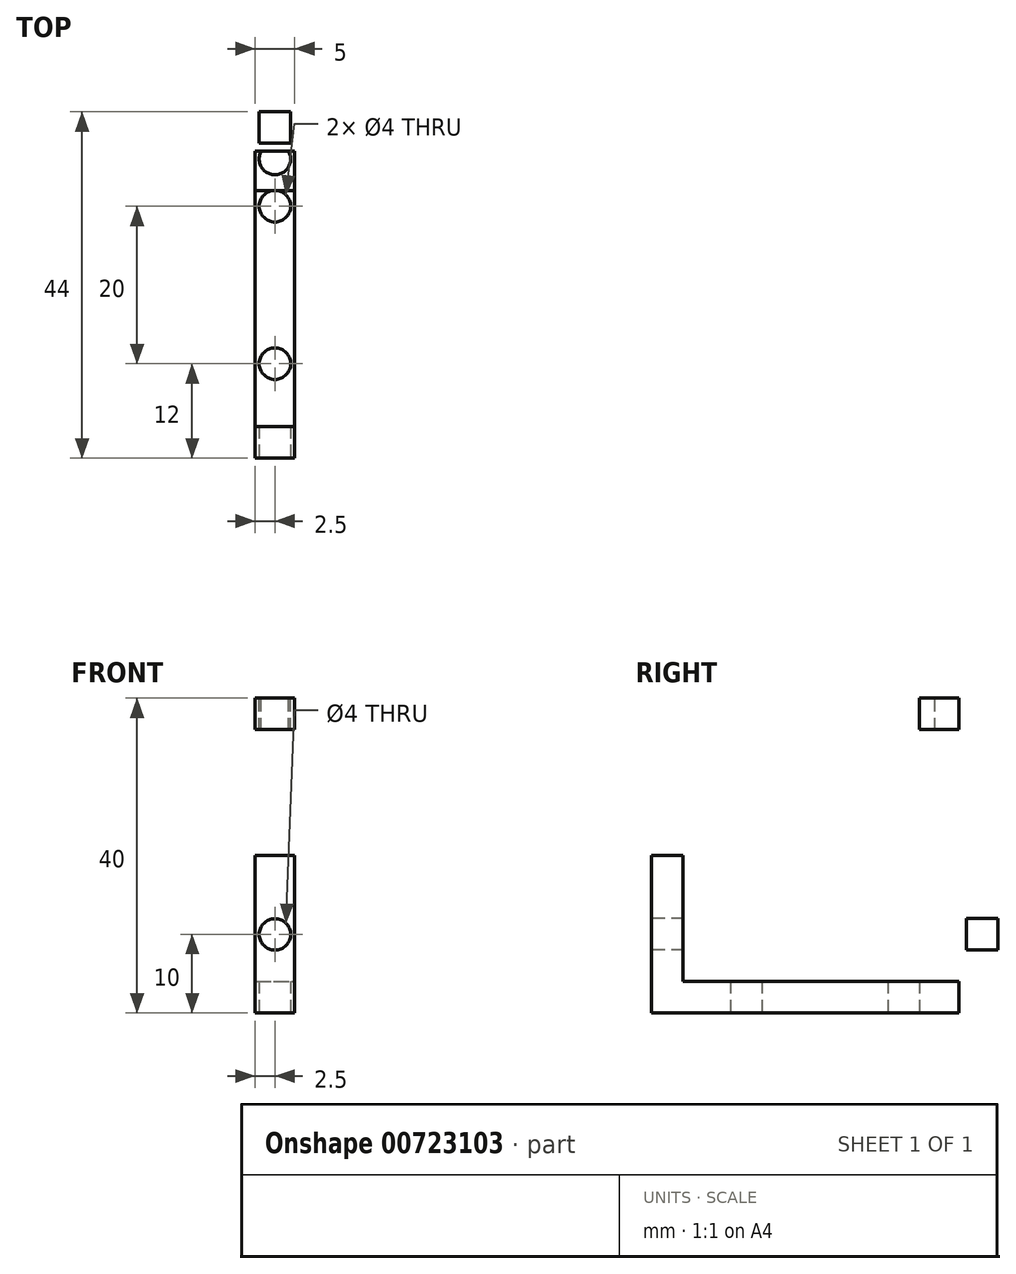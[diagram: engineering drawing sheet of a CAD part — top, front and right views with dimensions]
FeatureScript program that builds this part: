
annotation { "Feature Type Name" : "Feature", "Feature Type Description" : "" }
export const myFeature = defineFeature(function(context is Context, id is Id, definition is map)
    precondition{}
    {
        {
            var Q0;
            Q0=qCreatedBy(makeId("Right.planeOp"),FACE);
            var sketch = newSketch(context, id + "F0", { "sketchPlane" : qUnion([Q0])});
            skLineSegment(sketch, "E0.bottom", {"start": v(22, -20) * mm, "end": v(-22, -20) * mm});
            skLineSegment(sketch, "E0.top", {"start": v(22, 20) * mm, "end": v(12, 20) * mm});
            skLineSegment(sketch, "E0.left", {"start": v(22, -20) * mm, "end": v(22, 20) * mm});
            skLineSegment(sketch, "E0.right", {"start": v(-22, -20) * mm, "end": v(-22, 0) * mm});
            skPoint(sketch, "E0.middle", {"position": v(0, 0) * mm});
            skLineSegment(sketch, "E1.bottom", {"start": v(18, -16) * mm, "end": v(-18, -16) * mm});
            skLineSegment(sketch, "E1.top", {"start": v(18, 16) * mm, "end": v(12, 16) * mm});
            skLineSegment(sketch, "E1.left", {"start": v(18, -16) * mm, "end": v(18, 16) * mm});
            skLineSegment(sketch, "E1.right", {"start": v(-18, -16) * mm, "end": v(-18, 0) * mm});
            skLineSegment(sketch, "E2", {"start": v(12, 20) * mm, "end": v(12, 16) * mm});
            skLineSegment(sketch, "E3", {"start": v(-18, 0) * mm, "end": v(-22, 0) * mm});
            skPoint(sketch, "E4.trimOffspring.end.orphan", {"position": v(-22, 20) * mm});
            skPoint(sketch, "E5.start.orphan", {"position": v(-18, 16) * mm});
            skSolve(sketch);
        }
        {
            var Q0;
            Q0 = qSketchRegion(id + "F0", true);
            extrude(context, id + "F1", {"entities" : qUnion([Q0]), "endBound" : BoundingType.SYMMETRIC, "depth" : 5 * mm, "offsetDistance" : 25 * mm});
        }
        {
            var Q0;
            Q0=makeQuery(id+"F1.opExtrude","SWEPT_FACE",FACE,{"disambiguationData":[OSD([sQuery(id+"F0.wireOp",EDGE,"E0.top")])]});
            var sketch = newSketch(context, id + "F2", { "sketchPlane" : qUnion([Q0])});
            skCircle(sketch, "E6", {"center": v(0, 16) * mm, "radius": 2 * mm});
            skSolve(sketch);
        }
        {
            var Q0;
            Q0 = qSketchRegion(id + "F2", true);
            extrude(context, id + "F3", {"entities" : qUnion([Q0]), "operationType" : NewBodyOperationType.REMOVE, "oppositeDirection" : true, "depth" : 5 * mm, "offsetDistance" : 25 * mm});
        }
        {
            var Q0;
            Q0=makeQuery(id+"F1.opExtrude","SWEPT_FACE",FACE,{"disambiguationData":[OSD([sQuery(id+"F0.wireOp",EDGE,"E0.left")])]});
            var sketch = newSketch(context, id + "F4", { "sketchPlane" : qUnion([Q0])});
            skCircle(sketch, "E7", {"center": v(0, 10) * mm, "radius": 2 * mm});
            skCircle(sketch, "E8.MirrorC", {"center": v(0, -10) * mm, "radius": 2 * mm});
            skSolve(sketch);
        }
        {
            var Q0;
            Q0=makeQuery(id+"F4.imprint","IMPRINT",FACE,{"disambiguationData":[TD([[makeQuery(id+"F4.imprint","IMPRINT",EDGE,{"derivedFrom":sQuery(id+"F4.wireOp",EDGE,"E7")}),1.0]])]});
            var Q1;
            Q1=makeQuery(id+"F4.imprint","IMPRINT",FACE,{"disambiguationData":[TD([[makeQuery(id+"F4.imprint","IMPRINT",EDGE,{"derivedFrom":sQuery(id+"F4.wireOp",EDGE,"E8.MirrorC")}),-1.0]])]});
            extrude(context, id + "F5", {"entities" : qUnion([Q0, Q1]), "operationType" : NewBodyOperationType.REMOVE, "oppositeDirection" : true, "depth" : 5 * mm, "offsetDistance" : 25 * mm});
        }
        {
            var Q0;
            Q0=makeQuery(id+"F1.opExtrude","SWEPT_FACE",FACE,{"disambiguationData":[OSD([sQuery(id+"F0.wireOp",EDGE,"E0.right")])]});
            var sketch = newSketch(context, id + "F6", { "sketchPlane" : qUnion([Q0])});
            skCircle(sketch, "E9.MirrorC", {"center": v(0, -10) * mm, "radius": 2 * mm});
            skSolve(sketch);
        }
        {
            var Q0;
            Q0 = qSketchRegion(id + "F6", true);
            extrude(context, id + "F7", {"entities" : qUnion([Q0]), "operationType" : NewBodyOperationType.REMOVE, "oppositeDirection" : true, "depth" : 25 * mm, "offsetDistance" : 25 * mm});
        }
        {
            var Q0;
            Q0=makeQuery(id+"F1.opExtrude","SWEPT_FACE",FACE,{"disambiguationData":[OSD([sQuery(id+"F0.wireOp",EDGE,"E0.bottom")])]});
            var sketch = newSketch(context, id + "F8", { "sketchPlane" : qUnion([Q0])});
            skCircle(sketch, "E10", {"center": v(0, -10) * mm, "radius": 2 * mm});
            skCircle(sketch, "E11.MirrorC", {"center": v(0, 10) * mm, "radius": 2 * mm});
            skSolve(sketch);
        }
        {
            var Q0;
            Q0 = qSketchRegion(id + "F8", true);
            extrude(context, id + "F9", {"entities" : qUnion([Q0]), "operationType" : NewBodyOperationType.REMOVE, "oppositeDirection" : true, "depth" : 5 * mm, "offsetDistance" : 25 * mm});
        }
    });
